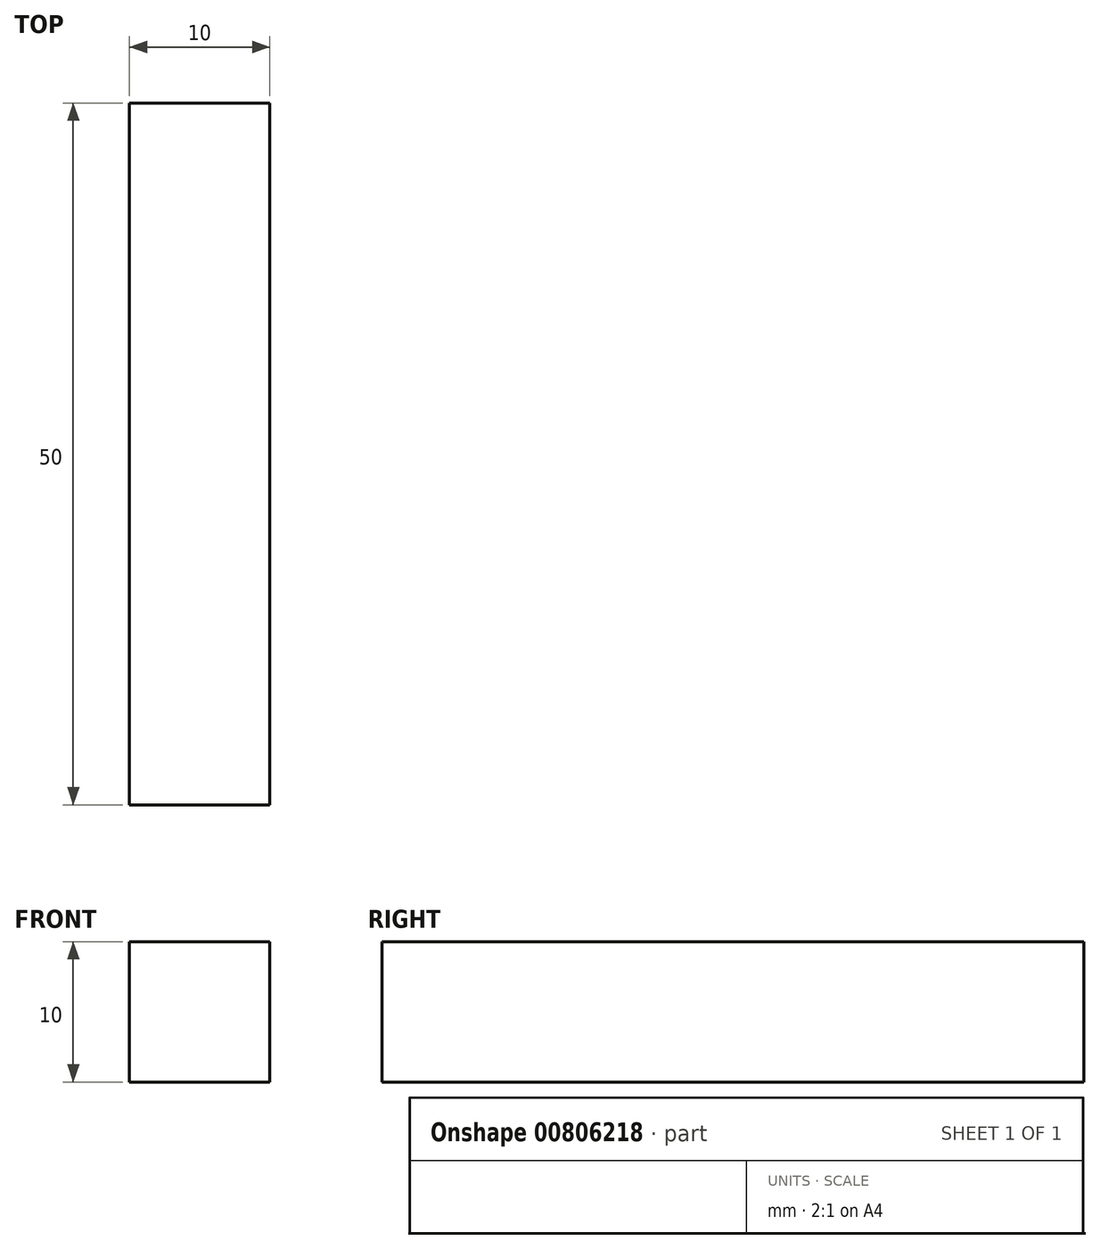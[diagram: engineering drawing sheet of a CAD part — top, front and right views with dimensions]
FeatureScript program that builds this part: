
annotation { "Feature Type Name" : "Feature", "Feature Type Description" : "" }
export const myFeature = defineFeature(function(context is Context, id is Id, definition is map)
    precondition{}
    {
        {
            var Q0;
            Q0=qCreatedBy(makeId("Top.planeOp"),FACE);
            var sketch = newSketch(context, id + "F0", { "sketchPlane" : qUnion([Q0])});
            skLineSegment(sketch, "E0.bottom", {"start": v(5, -25) * mm, "end": v(-5, -25) * mm});
            skLineSegment(sketch, "E0.top", {"start": v(5, 25) * mm, "end": v(-5, 25) * mm});
            skLineSegment(sketch, "E0.left", {"start": v(5, -25) * mm, "end": v(5, 25) * mm});
            skLineSegment(sketch, "E0.right", {"start": v(-5, -25) * mm, "end": v(-5, 25) * mm});
            skPoint(sketch, "E0.middle", {"position": v(0, 0) * mm});
            skSolve(sketch);
        }
        {
            var Q0;
            Q0=qSketchRegion(id+"F0",true);
            extrude(context, id + "F1", {"entities" : qUnion([Q0]), "depth" : 10 * mm, "offsetDistance" : 25 * mm});
        }
    });
